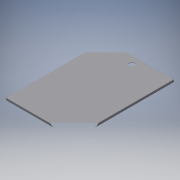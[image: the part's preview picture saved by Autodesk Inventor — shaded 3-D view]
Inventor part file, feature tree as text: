
AUTODESK INVENTOR PART (.ipt)
format: ipt  version: 2016 (Build 200138000, 138)  size: 331,264 bytes
history: native  units: mm
features: sheet_metal_op x16, other x8, sketch x7
ambient origin geometry x8: Origin, YZ Plane, XZ Plane, XY Plane, X Axis, Y Axis, Z Axis, Center Point
bodies: Solid1 (feature_tree)
feature tree (31):
  sheet_metal_op  "Face1"
  sheet_metal_op  "Flange1"
  sheet_metal_op  "Flange2"
  sheet_metal_op  "Flange3"
  sheet_metal_op  "Flange4"
  sheet_metal_op  "Flange5"
  sketch  "Sketch1"  dims[d0=258.0mm]
  other  "Plate1"
  sketch  "Sketch2"  dims[d1=376.0mm]
  other  "Plate2"
  sheet_metal_op  "Bend1"
  sheet_metal_op  "Corner1"
  sketch  "Sketch3"  dims[d2=1.2mm]
  other  "Plate3"
  sheet_metal_op  "Bend2"
  sheet_metal_op  "Corner2"
  sketch  "Sketch4"  dims[d3=1.2mm]
  other  "Plate4"
  sheet_metal_op  "Bend3"
  sheet_metal_op  "Corner3"
  sketch  "Sketch5"  dims[d4=0.6mm]
  other  "Plate5"
  sheet_metal_op  "Bend4"
  sheet_metal_op  "Corner4"
  sketch  "Sketch6"  dims[d5=2.4mm]
  other  "Plate6"
  sheet_metal_op  "Bend5"
  sheet_metal_op  "Corner5"
  sketch  "Sketch7"  dims[d6=1.2mm d7=10.0mm d8=90.0deg d9=1.2mm d10=4.8mm d11=1.2mm d12=1.2mm d13=1.2mm d14=0.6mm d15=2.4mm d16=1.2mm d17=10.0mm d18=90.0deg d19=1.2mm d20=4.8mm d21=1.2mm d22=1.2mm d23=1.2mm d24=0.6mm d25=2.4mm d26=1.2mm d27=10.0mm d28=90.0deg d29=1.2mm d30=4.8mm d31=1.2mm d32=1.2mm d33=1.2mm d34=0.6mm d35=2.4mm d36=1.2mm d37=10.0mm d38=90.0deg d39=1.2mm d40=4.8mm d41=1.2mm d42=1.2mm d43=1.2mm d44=0.6mm d45=2.4mm d46=1.2mm d47=5.0mm d48=90.0deg d49=1.2mm d50=4.8mm d51=1.2mm d52=1.2mm d54=30.0mm d55=1.2mm d56=0.0mm d57=16.5mm d58=10.3mm]
  other  "Cut1"
  other  "Definition1"
